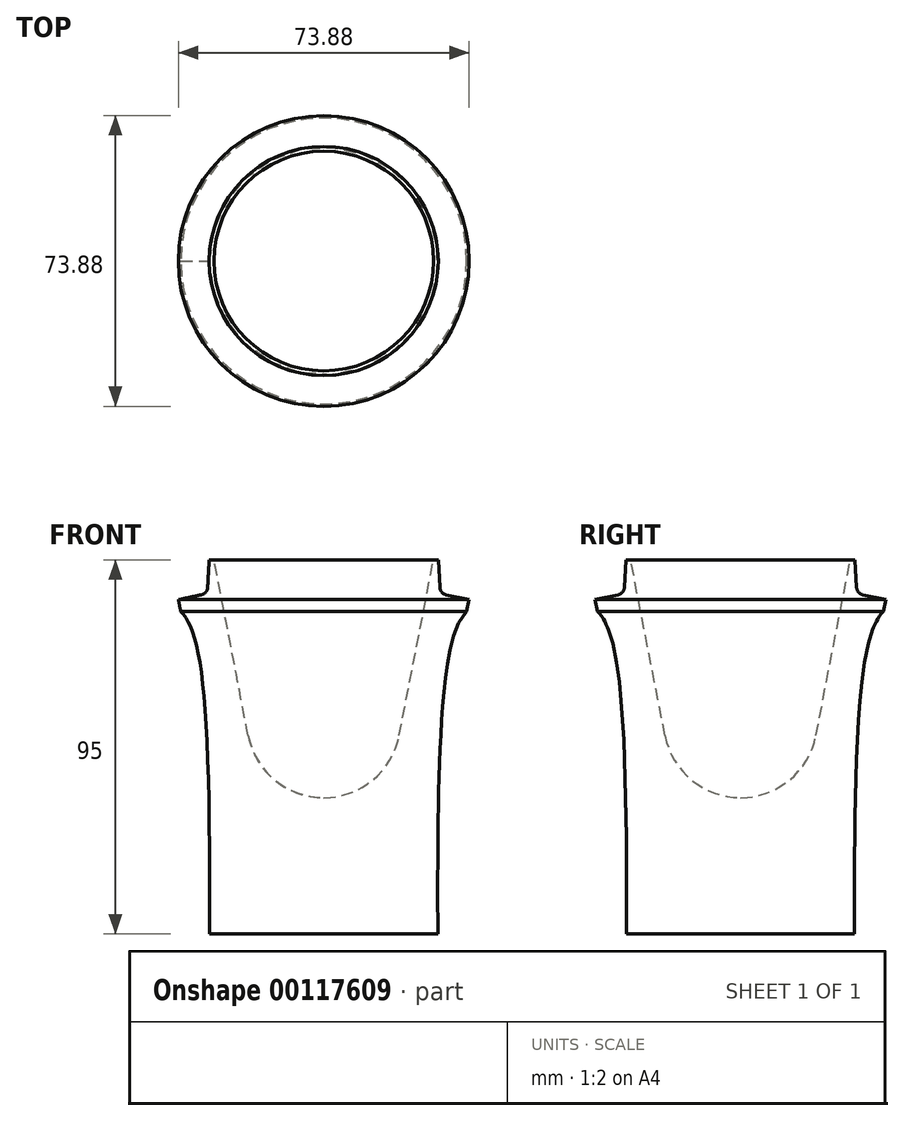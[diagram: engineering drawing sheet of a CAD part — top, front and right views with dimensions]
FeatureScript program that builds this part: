
annotation { "Feature Type Name" : "Feature", "Feature Type Description" : "" }
export const myFeature = defineFeature(function(context is Context, id is Id, definition is map)
    precondition{}
    {
        {
            var Q0;
            Q0=qCreatedBy(makeId("Front.planeOp"),FACE);
            var sketch = newSketch(context, id + "F0", { "sketchPlane" : qUnion([Q0])});
            skLineSegment(sketch, "E0", {"start": v(-29.1, 7) * mm, "end": v(-29.5, 0) * mm});
            skArc(sketch, "E1", {"start": v(-29.5, 0) * mm, "mid": v(-29.98, -1.19) * mm, "end": v(-31.08, -1.84) * mm});
            skLineSegment(sketch, "E2", {"start": v(-29.1, 7) * mm, "end": v(-27.9, 7) * mm});
            skLineSegment(sketch, "E3", {"start": v(-27.9, 7) * mm, "end": v(-19.17, -37.62) * mm});
            skLineSegment(sketch, "E4", {"start": v(-29, -88) * mm, "end": v(0, -88) * mm});
            skLineSegment(sketch, "E5", {"start": v(-29, -88) * mm, "end": v(-29, -80) * mm, "construction": true});
            skLineSegment(sketch, "E6", {"start": v(-31.08, -1.84) * mm, "end": v(-36.94, -3.1) * mm});
            skPoint(sketch, "E7.orphan", {"position": v(-33.5, 0) * mm});
            skLineSegment(sketch, "E8", {"start": v(-36.94, -3.1) * mm, "end": v(-36.32, -6.03) * mm});
            skFitSpline(sketch, "E9", {"points": [v(-36.32, -6.03) * mm, v(-29, -88) * mm], "startDerivative": vector(15.58, -16.38) * mm, "endDerivative": vector(-1.11, -184.34) * mm});
            skArc(sketch, "E10", {"start": v(-19.17, -37.62) * mm, "mid": v(-12.42, -48.95) * mm, "end": v(0, -53.4) * mm});
            skLineSegment(sketch, "E11", {"start": v(0, -88) * mm, "end": v(0, -53.4) * mm});
            skFitSpline(sketch, "E12", {"points": [v(-36.32, -6.03) * mm, v(-29, -80) * mm], "startDerivative": vector(15.58, -16.38) * mm, "endDerivative": vector(-34.03, -24.77) * mm, "construction": true});
            skLineSegment(sketch, "E13", {"start": v(-29, -80) * mm, "end": v(-29, -88) * mm, "construction": true});
            skSolve(sketch);
        }
        {
            var Q0;
            Q0 = qSketchRegion(id + "F0", true);
            var Q1;
            Q1=sQuery(id+"F0.wireOp",EDGE,"E11");
            revolve(context, id + "F1", {"surfaceOperationType" : NewSurfaceOperationType.NEW, "entities" : qUnion([Q0]), "axis" : qUnion([Q1]), "revolveType" : RevolveType.FULL});
        }
    });
